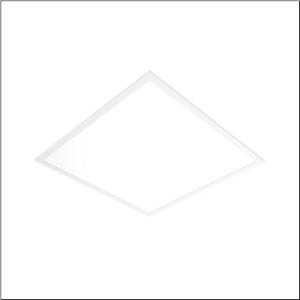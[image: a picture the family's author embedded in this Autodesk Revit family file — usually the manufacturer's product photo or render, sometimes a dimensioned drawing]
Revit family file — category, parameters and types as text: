
# Revit family: apollon_r__41_51mh11wd2n43_c469
name_source: partatom
category: Lighting Fixtures
units: mm (PartAtom-declared; Revit-internal decimal feet)

## family parameters
Cut with Voids When Loaded = No
Host = Face
Light Source = No
Part Type = Normal
Room Calculation Point = No
Round Connector Dimension = Use Diameter
Shared = No

## types (1)
- --- (1 x LED, 3450 lm, 28.5 W, 6500K)
    Apparent Load = 29 VA
    CIE Flux Codes = 61 87 97 100 100
    Color Rendering = 80
    Color Temperature = 6500K
    Default Elevation = 1800 mm
    Description = Apollon® 41, office luminaire, primary optical cover: prismatic diffuser, of PS, light emission: direct distribution, primary light characteristic: symmetric, installation type: lay-in mounting, LED, rated luminous flux: 3.500lm, luminous efficacy: 123lm/W, light colour: 840/865, colour temperature: 4000/6500K, with terminal, 5-pole, mains connection: 220..240V, AC/DC, 0/50..60Hz, housing, of aluminium section, traffic white (RAL 9016), module: M625, length: 620mm, width: 620mm, height: 28mm, housing upper side, of sheet steel, protection rating (complete): IP20, protection rating (lamp compartment, on room side): IP40, insulation class (complete): insulation class II (safety insulation), certification: CE, ENEC, permissible operating ambient temperature: -25..+40°C, packaging unit: 1 piece
    Height = 0 mm  [stored 0 ft]
    Lamp = 1 x LED
    Lamp Light Flux = 3450 lm
    Lamp Power = 28.5 W
    Lamp count = 1
    Length = 620 mm
    Luminous efficacy = 121 lm/W
    Manufacturer = Siteco
    ModVariant = No
    Model = 51MH11WD2N43
    Mounting Place = Ceiling
    Mounting Type = Recessed
    Number of Poles = 1
    OnlyDefault = Yes
    Power Factor = 1
    Product Name = Apollon® 41
    Product group = office luminaire | ceiling recessed
    ProductGroupID = 401
    Protection Class = Protection class II
    Protection Degree = IP 20
    RLX_Detail_Level = 1
    RLX_Emergency_Light_Flux = 0 lm
    RLX_Emergency_Type = 0
    RLX_Emergency_Type_DB = No
    RlxData = <blob elided: 12397 chars, md5=5e13d0cc>
    Socket = socket
    Standby Power = 0 W
    System Light Flux = 3450 lm
    System Power = 29 W
    Type Comments = individual setting
    Type Image = l_1291024.jpg
    URL = http://relux.com
    VarID = @adj_027741
    Voltage = 0 V
    Weight = 0.00 kg
    Width = 620 mm

note: [stored X ft] marks values corroborated as IEEE doubles in the binary element streams (Revit-internal decimal feet)

## geometry (parser evidence)
native form markers: Sweep x9
no freeform markers — native parametric forms only
